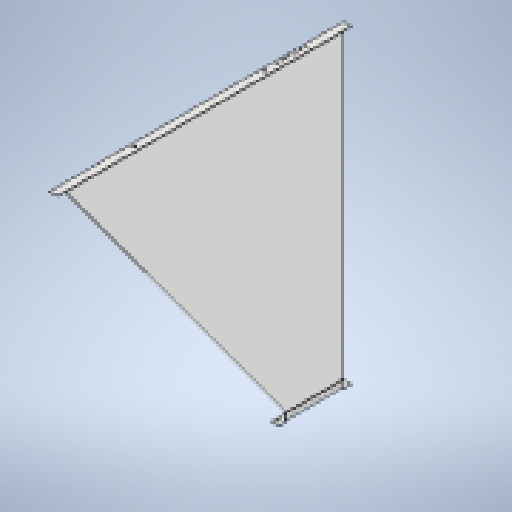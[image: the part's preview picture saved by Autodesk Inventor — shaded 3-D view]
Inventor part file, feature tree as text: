
AUTODESK INVENTOR PART (.ipt)
format: ipt  version: 2025.1 (Build 291241020, 241B)  size: 438,272 bytes
history: native  units: mm
features: sheet_metal_op x9, sketch x8, other x8, extrude x2, projected_geometry x2, mirror x1, pattern_linear x1
ambient origin geometry x8: Origin, YZ Plane, XZ Plane, XY Plane, X Axis, Y Axis, Z Axis, Center Point
bodies: Solid1 (feature_tree)
feature tree (31):
  sheet_metal_op  "Contour Flange1"
  extrude  "Extrusion10"  Depth=3.0mm
  mirror  "Mirror1"
  sketch  "Sketch16"  dims[d10=5.0mm d11=1700.0mm]
  extrude  "Extrusion11"  Depth=6.0mm
  other  "Mark3"
  other  "A-Side Definition"
  sheet_metal_op  "Flange3"
  sheet_metal_op  "Flange4"
  pattern_linear  "Rectangular Pattern1"  Count1=170  [1 undecoded]
  sketch  "Sketch1"  dims[d6=3.0mm d7=3.0mm]
  other  "Plate1"
  sheet_metal_op  "Bend1"
  sheet_metal_op  "Corner1"
  sketch  "Sketch15"  dims[d8=1.5mm d9=6.0mm]
  projected_geometry  "Projected Loop9"
  sketch  "Sketch17"  dims[d12=5.0mm]
  projected_geometry  "Projected Loop10"
  sketch  "Sketch18"  dims[d13=4.0mm]
  other  "Plate4"
  sheet_metal_op  "Bend4"
  sheet_metal_op  "Corner4"
  sketch  "Sketch19"  dims[d14=12.0mm]
  other  "Plate5"
  sheet_metal_op  "Bend5"
  sheet_metal_op  "Corner5"
  sketch  "Sketch20"  dims[d15=3.0mm]
  sketch  "Sketch21"  dims[d16=5.0mm d65=0.0mm d66=1170.0mm d68=50.0mm d70=5.0mm d79=875.499815mm d84=120.0deg d85=50.0mm d86=0.0mm d87=11.059943mm d88=2.0mm d89=0.0mm d90=0.0mm d91=200.0mm d92=350.0mm d93=3.0mm d94=1.5mm d95=6.0mm d96=5.0mm d97=50.0mm d98=30.0deg d99=5.0mm d100=12.0mm d101=3.0mm d102=5.0mm d103=3.0mm d104=1.5mm d105=6.0mm d106=5.0mm d107=45.0mm d108=90.0deg d109=5.0mm d110=12.0mm d111=3.0mm d112=5.0mm d113=14.0mm d114=15.0mm d115=3.0mm d116=0.0mm d117=30.0mm d119=195.0mm d120=-45.0mm d121=-45.0mm d122=16.0mm d123=800.0mm d124=20.0mm d125=3.0mm d126=0.0mm]
  other  "Cut1"
  other  "Cut2"
  other  "Definition1"
note: 1 required parameter value undecoded (feature->parameter linkage not recoverable at this tier; creation-order binding heuristic only, values carry confidence <= 0.55)
